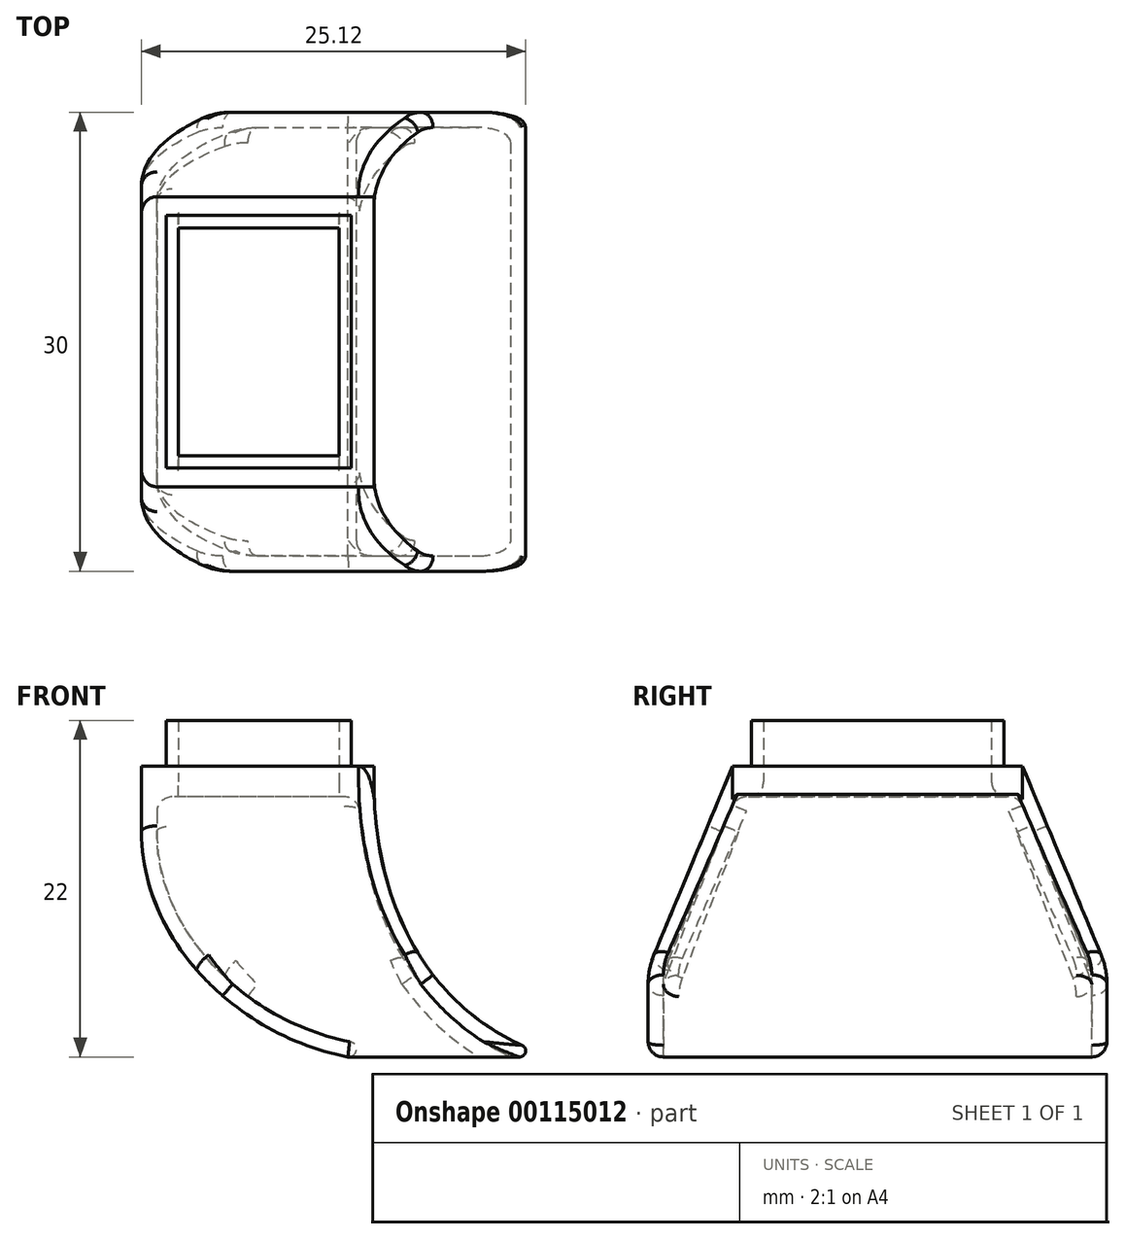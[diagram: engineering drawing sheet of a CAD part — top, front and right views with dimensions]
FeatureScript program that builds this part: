
annotation { "Feature Type Name" : "Feature", "Feature Type Description" : "" }
export const myFeature = defineFeature(function(context is Context, id is Id, definition is map)
    precondition{}
    {
        {
            var Q0;
            Q0=qCreatedBy(makeId("Front.planeOp"),FACE);
            var sketch = newSketch(context, id + "F0", { "sketchPlane" : qUnion([Q0])});
            skLineSegment(sketch, "E0.top", {"start": v(0, -19) * mm, "end": v(27, -19) * mm, "construction": true});
            skLineSegment(sketch, "E0.right", {"start": v(27, 0) * mm, "end": v(27, -19) * mm, "construction": true});
            skLineSegment(sketch, "E1", {"start": v(0, 0) * mm, "end": v(0, -4.28) * mm});
            skLineSegment(sketch, "E2", {"start": v(0, 0) * mm, "end": v(15.2, 0) * mm});
            skFitSpline(sketch, "E3", {"points": [v(0, -4.28) * mm, v(13.5, -19) * mm], "startDerivative": vector(0, -21.34) * mm, "endDerivative": vector(21.8, -4.21) * mm});
            skFitSpline(sketch, "E4", {"points": [v(15.2, 0) * mm, v(27, -19) * mm], "startDerivative": vector(-0.94, -28.86) * mm, "endDerivative": vector(22.74, -6.41) * mm});
            skLineSegment(sketch, "E5", {"start": v(13.5, -19) * mm, "end": v(27, -19) * mm});
            skSolve(sketch);
        }
        {
            var Q0;
            Q0 = qSketchRegion(id + "F0", true);
            extrude(context, id + "F1", {"entities" : qUnion([Q0]), "endBound" : BoundingType.SYMMETRIC, "depth" : 30 * mm});
        }
        {
            var Q0;
            Q0=qCreatedBy(makeId("Right.planeOp"),FACE);
            var sketch = newSketch(context, id + "F2", { "sketchPlane" : qUnion([Q0])});
            skLineSegment(sketch, "E6", {"start": v(-9.48, 0) * mm, "end": v(-16.87, -17.72) * mm});
            skLineSegment(sketch, "E7.MirrorCS", {"start": v(9.48, 0) * mm, "end": v(16.87, -17.72) * mm});
            skLineSegment(sketch, "E8", {"start": v(-16.87, -17.72) * mm, "end": v(-16.87, 6.12) * mm});
            skLineSegment(sketch, "E9", {"start": v(-16.87, 6.12) * mm, "end": v(22.97, 6.12) * mm});
            skLineSegment(sketch, "E10", {"start": v(22.97, 6.12) * mm, "end": v(16.87, -17.72) * mm});
            skLineSegment(sketch, "E11", {"start": v(-9.48, 0) * mm, "end": v(9.48, 0) * mm});
            skSolve(sketch);
        }
        {
            var Q0;
            Q0 = qSketchRegion(id + "F2", true);
            extrude(context, id + "F3", {"entities" : qUnion([Q0]), "operationType" : NewBodyOperationType.REMOVE, "endBound" : BoundingType.SYMMETRIC, "oppositeDirection" : true, "depth" : 100 * mm});
        }
        {
            var Q0;
            Q0=makeQuery(id+"F3.boolean.opBoolean","INTERSECT",EDGE,{"derivedFrom":[makeQuery(id+"F1.opExtrude","CAP_FACE",FACE,{"disambiguationData":[OSD([sQuery(id+"F0.wireOp",EDGE,"E1"),sQuery(id+"F0.wireOp",EDGE,"E2"),sQuery(id+"F0.wireOp",EDGE,"E3"),sQuery(id+"F0.wireOp",EDGE,"E4"),sQuery(id+"F0.wireOp",EDGE,"E5")])],"isStart":false}),makeQuery(id+"F3.opExtrude","SWEPT_FACE",FACE,{"disambiguationData":[OSD([sQuery(id+"F2.wireOp",EDGE,"E6")])]})]});
            var Q1;
            Q1=makeQuery(id+"F3.boolean.opBoolean","INTERSECT",EDGE,{"derivedFrom":[makeQuery(id+"F1.opExtrude","CAP_FACE",FACE,{"disambiguationData":[OSD([sQuery(id+"F0.wireOp",EDGE,"E1"),sQuery(id+"F0.wireOp",EDGE,"E2"),sQuery(id+"F0.wireOp",EDGE,"E3"),sQuery(id+"F0.wireOp",EDGE,"E4"),sQuery(id+"F0.wireOp",EDGE,"E5")])],"isStart":true}),makeQuery(id+"F3.opExtrude","SWEPT_FACE",FACE,{"disambiguationData":[OSD([sQuery(id+"F2.wireOp",EDGE,"E7.MirrorCS")])]})]});
            fillet(context, id + "F4", {"entities" : qUnion([Q0, Q1]), "radius" : 5 * mm, "tangentPropagation" : true, "allowEdgeOverflow" : false});
        }
        {
            var Q0;
            Q0=makeQuery(id+"F1.opExtrude","SWEPT_FACE",FACE,{"disambiguationData":[OSD([sQuery(id+"F0.wireOp",EDGE,"E5")])]});
            var Q1;
            Q1=makeQuery(id+"F1.opExtrude","SWEPT_FACE",FACE,{"disambiguationData":[OSD([sQuery(id+"F0.wireOp",EDGE,"E2")])]});
            shell(context, id + "F5", {"entities" : qUnion([Q0, Q1]), "thickness" : 1 * mm});
        }
        {
            var Q0;
            Q0=makeQuery(id+"F5.opShell","OFFSET_EDGE",EDGE,{"disambiguationData":[OSD([sQuery(id+"F0.wireOp",EDGE,"E3"),sQuery(id+"F0.wireOp",EDGE,"E5")])]});
            fillet(context, id + "F6", {"entities" : qUnion([Q0]), "radius" : 0.5 * mm, "tangentPropagation" : true, "allowEdgeOverflow" : false});
        }
        {
            var Q0;
            Q0=makeQuery(id+"F1.opExtrude","SWEPT_EDGE",EDGE,{"disambiguationData":[OSD([sQuery(id+"F0.wireOp",EDGE,"E4"),sQuery(id+"F0.wireOp",EDGE,"E5")])]});
            fillet(context, id + "F7", {"entities" : qUnion([Q0]), "radius" : 0.4 * mm, "tangentPropagation" : true, "allowEdgeOverflow" : false});
        }
        {
            var Q0;
            Q0=makeQuery(id+"F1.opExtrude","SWEPT_FACE",FACE,{"disambiguationData":[OSD([sQuery(id+"F0.wireOp",EDGE,"E2")])]});
            var sketch = newSketch(context, id + "F8", { "sketchPlane" : qUnion([Q0])});
            skLineSegment(sketch, "E12.bottom", {"start": v(13.72, -8.25) * mm, "end": v(1.62, -8.25) * mm});
            skLineSegment(sketch, "E12.top", {"start": v(13.72, 8.25) * mm, "end": v(1.62, 8.25) * mm});
            skLineSegment(sketch, "E12.left", {"start": v(13.72, -8.25) * mm, "end": v(13.72, 8.25) * mm});
            skLineSegment(sketch, "E12.right", {"start": v(1.62, -8.25) * mm, "end": v(1.62, 8.25) * mm});
            skPoint(sketch, "E12.middle", {"position": v(7.67, 0) * mm});
            skPoint(sketch, "E12.middle.positionSnap0", {"position": v(15.2, 0) * mm});
            skPoint(sketch, "E12.centerSnap0", {"position": v(15.2, 0) * mm});
            skLineSegment(sketch, "E13.bottom", {"start": v(15.2, -9.48) * mm, "end": v(0.14, -9.48) * mm});
            skLineSegment(sketch, "E13.top", {"start": v(15.2, 9.48) * mm, "end": v(0.14, 9.48) * mm});
            skLineSegment(sketch, "E13.left", {"start": v(15.2, -9.48) * mm, "end": v(15.2, 9.48) * mm});
            skLineSegment(sketch, "E13.right", {"start": v(0.14, -9.48) * mm, "end": v(0.14, 9.48) * mm});
            skSolve(sketch);
        }
        {
            var Q0;
            Q0 = qSketchRegion(id + "F8", true);
            extrude(context, id + "F9", {"entities" : qUnion([Q0]), "operationType" : NewBodyOperationType.ADD, "oppositeDirection" : true, "depth" : 2 * mm});
        }
        {
            var Q0;
            Q0=makeQuery(id+"F9.boolean.opBoolean","MERGE",FACE,{"derivedFrom":[makeQuery(id+"F1.opExtrude","SWEPT_FACE",FACE,{"disambiguationData":[OSD([sQuery(id+"F0.wireOp",EDGE,"E2")])]}),makeQuery(id+"F9.opExtrude","CAP_FACE",FACE,{"disambiguationData":[OSD([sQuery(id+"F8.wireOp",EDGE,"E12.bottom"),sQuery(id+"F8.wireOp",EDGE,"E12.top"),sQuery(id+"F8.wireOp",EDGE,"E12.left"),sQuery(id+"F8.wireOp",EDGE,"E12.right"),sQuery(id+"F8.wireOp",EDGE,"E13.bottom"),sQuery(id+"F8.wireOp",EDGE,"E13.top"),sQuery(id+"F8.wireOp",EDGE,"E13.left"),sQuery(id+"F8.wireOp",EDGE,"E13.right")])],"isStart":true})]});
            var sketch = newSketch(context, id + "F10", { "sketchPlane" : qUnion([Q0])});
            skLineSegment(sketch, "E14.0", {"start": v(13.72, -8.25) * mm, "end": v(13.72, 8.25) * mm});
            skLineSegment(sketch, "E15.0", {"start": v(13.72, -8.25) * mm, "end": v(1.62, -8.25) * mm});
            skLineSegment(sketch, "E16.0", {"start": v(13.72, 8.25) * mm, "end": v(1.62, 8.25) * mm});
            skLineSegment(sketch, "E17.0", {"start": v(1.62, -8.25) * mm, "end": v(1.62, 8.25) * mm});
            skLineSegment(sketch, "E18.0", {"start": v(2.42, -7.45) * mm, "end": v(2.42, 7.45) * mm});
            skLineSegment(sketch, "E18.1", {"start": v(12.92, -7.45) * mm, "end": v(2.42, -7.45) * mm});
            skLineSegment(sketch, "E18.2", {"start": v(12.92, -7.45) * mm, "end": v(12.92, 7.45) * mm});
            skLineSegment(sketch, "E18.3", {"start": v(12.92, 7.45) * mm, "end": v(2.42, 7.45) * mm});
            skSolve(sketch);
        }
        {
            var Q0;
            Q0 = qSketchRegion(id + "F10", true);
            extrude(context, id + "F11", {"entities" : qUnion([Q0]), "operationType" : NewBodyOperationType.ADD, "endBound" : BoundingType.SYMMETRIC, "depth" : 4 * mm});
        }
        {
            var Q0;
            Q0=makeQuery(id+"F9.boolean.opBoolean","INTERSECT",EDGE,{"derivedFrom":[makeQuery(id+"F5.opShell","OFFSET_FACE",FACE,{"disambiguationData":[OSD([sQuery(id+"F2.wireOp",EDGE,"E7.MirrorCS")])]}),makeQuery(id+"F9.opExtrude","CAP_FACE",FACE,{"disambiguationData":[OSD([sQuery(id+"F8.wireOp",EDGE,"E12.bottom"),sQuery(id+"F8.wireOp",EDGE,"E12.top"),sQuery(id+"F8.wireOp",EDGE,"E12.left"),sQuery(id+"F8.wireOp",EDGE,"E12.right"),sQuery(id+"F8.wireOp",EDGE,"E13.bottom"),sQuery(id+"F8.wireOp",EDGE,"E13.top"),sQuery(id+"F8.wireOp",EDGE,"E13.left"),sQuery(id+"F8.wireOp",EDGE,"E13.right")])],"isStart":false})]});
            var Q1;
            Q1=makeQuery(id+"F9.boolean.opBoolean","INTERSECT",EDGE,{"derivedFrom":[makeQuery(id+"F5.opShell","OFFSET_FACE",FACE,{"disambiguationData":[OSD([sQuery(id+"F0.wireOp",EDGE,"E1")])]}),makeQuery(id+"F9.opExtrude","CAP_FACE",FACE,{"disambiguationData":[OSD([sQuery(id+"F8.wireOp",EDGE,"E12.bottom"),sQuery(id+"F8.wireOp",EDGE,"E12.top"),sQuery(id+"F8.wireOp",EDGE,"E12.left"),sQuery(id+"F8.wireOp",EDGE,"E12.right"),sQuery(id+"F8.wireOp",EDGE,"E13.bottom"),sQuery(id+"F8.wireOp",EDGE,"E13.top"),sQuery(id+"F8.wireOp",EDGE,"E13.left"),sQuery(id+"F8.wireOp",EDGE,"E13.right")])],"isStart":false})]});
            var Q2;
            Q2=makeQuery(id+"F9.boolean.opBoolean","INTERSECT",EDGE,{"derivedFrom":[makeQuery(id+"F5.opShell","OFFSET_FACE",FACE,{"disambiguationData":[OSD([sQuery(id+"F2.wireOp",EDGE,"E6")])]}),makeQuery(id+"F9.opExtrude","CAP_FACE",FACE,{"disambiguationData":[OSD([sQuery(id+"F8.wireOp",EDGE,"E12.bottom"),sQuery(id+"F8.wireOp",EDGE,"E12.top"),sQuery(id+"F8.wireOp",EDGE,"E12.left"),sQuery(id+"F8.wireOp",EDGE,"E12.right"),sQuery(id+"F8.wireOp",EDGE,"E13.bottom"),sQuery(id+"F8.wireOp",EDGE,"E13.top"),sQuery(id+"F8.wireOp",EDGE,"E13.left"),sQuery(id+"F8.wireOp",EDGE,"E13.right")])],"isStart":false})]});
            var Q3;
            Q3=makeQuery(id+"F5.opShell","OFFSET_EDGE",EDGE,{"disambiguationData":[OSD([sQuery(id+"F0.wireOp",EDGE,"E1"),sQuery(id+"F2.wireOp",EDGE,"E6")])]});
            var Q4;
            Q4=makeQuery(id+"F5.opShell","OFFSET_EDGE",EDGE,{"disambiguationData":[OSD([sQuery(id+"F0.wireOp",EDGE,"E3"),sQuery(id+"F2.wireOp",EDGE,"E7.MirrorCS")])]});
            var Q5;
            Q5=makeQuery(id+"F9.boolean.opBoolean","INTERSECT",EDGE,{"derivedFrom":[makeQuery(id+"F5.opShell","OFFSET_FACE",FACE,{"disambiguationData":[OSD([sQuery(id+"F0.wireOp",EDGE,"E4")])]}),makeQuery(id+"F9.opExtrude","CAP_FACE",FACE,{"disambiguationData":[OSD([sQuery(id+"F8.wireOp",EDGE,"E12.bottom"),sQuery(id+"F8.wireOp",EDGE,"E12.top"),sQuery(id+"F8.wireOp",EDGE,"E12.left"),sQuery(id+"F8.wireOp",EDGE,"E12.right"),sQuery(id+"F8.wireOp",EDGE,"E13.bottom"),sQuery(id+"F8.wireOp",EDGE,"E13.top"),sQuery(id+"F8.wireOp",EDGE,"E13.left"),sQuery(id+"F8.wireOp",EDGE,"E13.right")])],"isStart":false})]});
            fillet(context, id + "F12", {"entities" : qUnion([Q0, Q1, Q2, Q3, Q4, Q5]), "radius" : 1 * mm, "tangentPropagation" : true, "allowEdgeOverflow" : false});
        }
        {
            var Q0;
            Q0=makeQuery(id+"F11.opExtrude","CAP_EDGE",EDGE,{"disambiguationData":[OSD([sQuery(id+"F10.wireOp",EDGE,"E18.3")])],"isStart":true});
            var Q1;
            Q1=makeQuery(id+"F11.opExtrude","CAP_EDGE",EDGE,{"disambiguationData":[OSD([sQuery(id+"F10.wireOp",EDGE,"E18.1")])],"isStart":true});
            fillet(context, id + "F13", {"entities" : qUnion([Q0, Q1]), "radius" : 1 * mm, "tangentPropagation" : true, "allowEdgeOverflow" : false});
        }
        {
            var Q0;
            {var subQ0=sQuery(id+"F0.wireOp",EDGE,"E4");Q0=makeQuery(id+"F5.opShell","OFFSET_EDGE",EDGE,{"disambiguationData":[OSD([subQ0]),TDD([makeQuery(id+"F1.opExtrude","CAP_EDGE",EDGE,{"disambiguationData":[OSD([subQ0])],"isStart":false})])]});}
            var Q1;
            {var subQ0=sQuery(id+"F0.wireOp",EDGE,"E4");Q1=makeQuery(id+"F5.opShell","OFFSET_EDGE",EDGE,{"disambiguationData":[OSD([subQ0]),TDD([makeQuery(id+"F1.opExtrude","CAP_EDGE",EDGE,{"disambiguationData":[OSD([subQ0])],"isStart":true})])]});}
            var Q2;
            Q2=makeQuery(id+"F3.boolean.opBoolean","INTERSECT",EDGE,{"derivedFrom":[makeQuery(id+"F1.opExtrude","SWEPT_FACE",FACE,{"disambiguationData":[OSD([sQuery(id+"F0.wireOp",EDGE,"E4")])]}),makeQuery(id+"F3.opExtrude","SWEPT_FACE",FACE,{"disambiguationData":[OSD([sQuery(id+"F2.wireOp",EDGE,"E6")])]})]});
            var Q3;
            Q3=makeQuery(id+"F3.boolean.opBoolean","INTERSECT",EDGE,{"derivedFrom":[makeQuery(id+"F1.opExtrude","SWEPT_FACE",FACE,{"disambiguationData":[OSD([sQuery(id+"F0.wireOp",EDGE,"E4")])]}),makeQuery(id+"F3.opExtrude","SWEPT_FACE",FACE,{"disambiguationData":[OSD([sQuery(id+"F2.wireOp",EDGE,"E7.MirrorCS")])]})]});
            var Q4;
            Q4=makeQuery(id+"F3.boolean.opBoolean","INTERSECT",EDGE,{"derivedFrom":[makeQuery(id+"F1.opExtrude","SWEPT_FACE",FACE,{"disambiguationData":[OSD([sQuery(id+"F0.wireOp",EDGE,"E3")])]}),makeQuery(id+"F3.opExtrude","SWEPT_FACE",FACE,{"disambiguationData":[OSD([sQuery(id+"F2.wireOp",EDGE,"E6")])]})]});
            var Q5;
            Q5=makeQuery(id+"F3.boolean.opBoolean","INTERSECT",EDGE,{"derivedFrom":[makeQuery(id+"F1.opExtrude","SWEPT_FACE",FACE,{"disambiguationData":[OSD([sQuery(id+"F0.wireOp",EDGE,"E3")])]}),makeQuery(id+"F3.opExtrude","SWEPT_FACE",FACE,{"disambiguationData":[OSD([sQuery(id+"F2.wireOp",EDGE,"E7.MirrorCS")])]})]});
            fillet(context, id + "F14", {"entities" : qUnion([Q0, Q1, Q2, Q3, Q4, Q5]), "radius" : 1 * mm, "tangentPropagation" : true, "allowEdgeOverflow" : false});
        }
        {
            var Q0;
            Q0=makeQuery(id+"F11.opExtrude","CAP_FACE",FACE,{"disambiguationData":[OSD([sQuery(id+"F10.wireOp",EDGE,"E14.0"),sQuery(id+"F10.wireOp",EDGE,"E15.0"),sQuery(id+"F10.wireOp",EDGE,"E16.0"),sQuery(id+"F10.wireOp",EDGE,"E17.0"),sQuery(id+"F10.wireOp",EDGE,"E18.0"),sQuery(id+"F10.wireOp",EDGE,"E18.1"),sQuery(id+"F10.wireOp",EDGE,"E18.2"),sQuery(id+"F10.wireOp",EDGE,"E18.3")])],"isStart":false});
            extrude(context, id + "F15", {"entities" : qUnion([Q0]), "operationType" : NewBodyOperationType.ADD, "depth" : 1 * mm});
        }
    });
